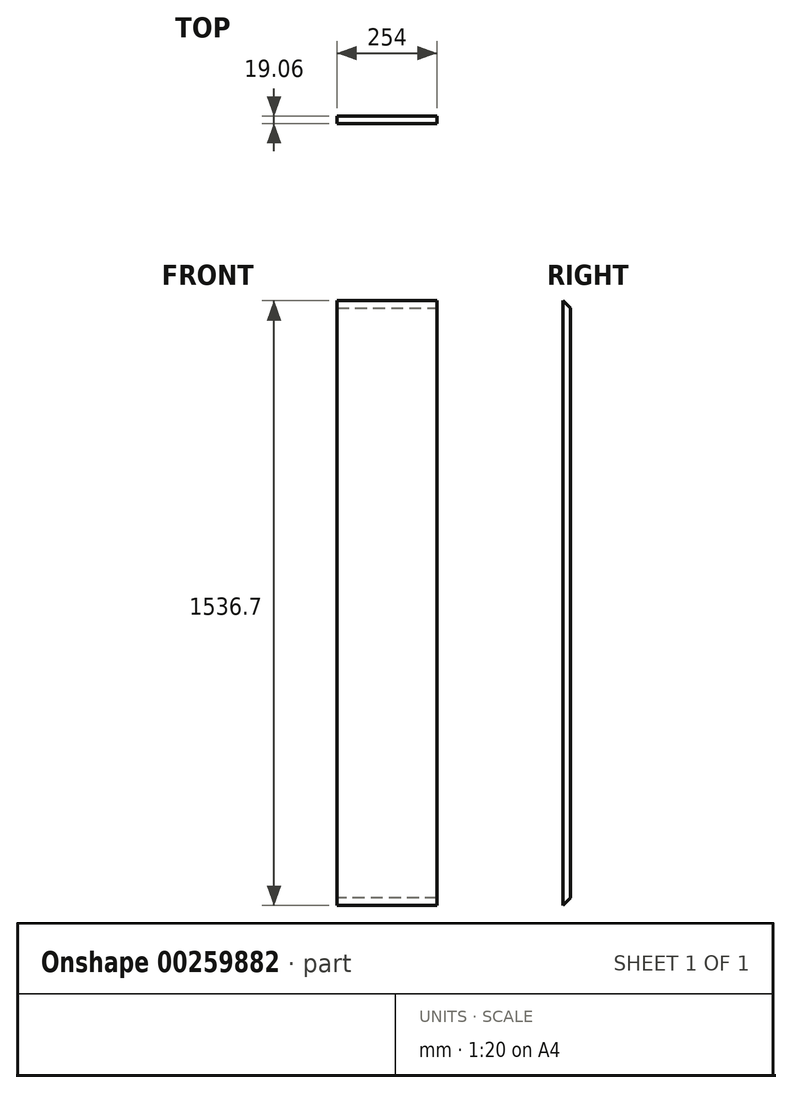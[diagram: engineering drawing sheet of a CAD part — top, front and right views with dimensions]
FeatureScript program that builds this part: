
annotation { "Feature Type Name" : "Feature", "Feature Type Description" : "" }
export const myFeature = defineFeature(function(context is Context, id is Id, definition is map)
    precondition{}
    {
        {
            var Q0;
            Q0=qCreatedBy(makeId("Top.planeOp"),FACE);
            var sketch = newSketch(context, id + "F0", { "sketchPlane" : qUnion([Q0])});
            skLineSegment(sketch, "E0.bottom", {"start": v(-127, 9.53) * mm, "end": v(127, 9.53) * mm});
            skLineSegment(sketch, "E0.top", {"start": v(-127, -9.53) * mm, "end": v(127, -9.53) * mm});
            skLineSegment(sketch, "E0.left", {"start": v(-127, 9.52) * mm, "end": v(-127, -9.53) * mm});
            skLineSegment(sketch, "E0.right", {"start": v(127, 9.53) * mm, "end": v(127, -9.52) * mm});
            skSolve(sketch);
        }
        {
            var Q0;
            Q0=makeQuery(id+"F0.imprint","IMPRINT",FACE,{"disambiguationData":[TD([[makeQuery(id+"F0.imprint","IMPRINT",EDGE,{"derivedFrom":sQuery(id+"F0.wireOp",EDGE,"E0.bottom")}),-1.0]])]});
            extrude(context, id + "F1", {"entities" : qUnion([Q0]), "endBound" : BoundingType.SYMMETRIC, "depth" : 1536.7 * mm});
        }
        {
            var Q0;
            Q0=makeQuery(id+"F1.opExtrude","CAP_EDGE",EDGE,{"disambiguationData":[OSD([sQuery(id+"F0.wireOp",EDGE,"E0.bottom")])],"isStart":false});
            var Q1;
            Q1=makeQuery(id+"F1.opExtrude","CAP_EDGE",EDGE,{"disambiguationData":[OSD([sQuery(id+"F0.wireOp",EDGE,"E0.bottom")])],"isStart":true});
            chamfer(context, id + "F2", {"entities" : qUnion([Q0, Q1]), "chamferType" : ChamferType.OFFSET_ANGLE, "width" : 19.05 * mm, "oppositeDirection" : false, "angle" : 45 * degree, "tangentPropagation" : true});
        }
    });
